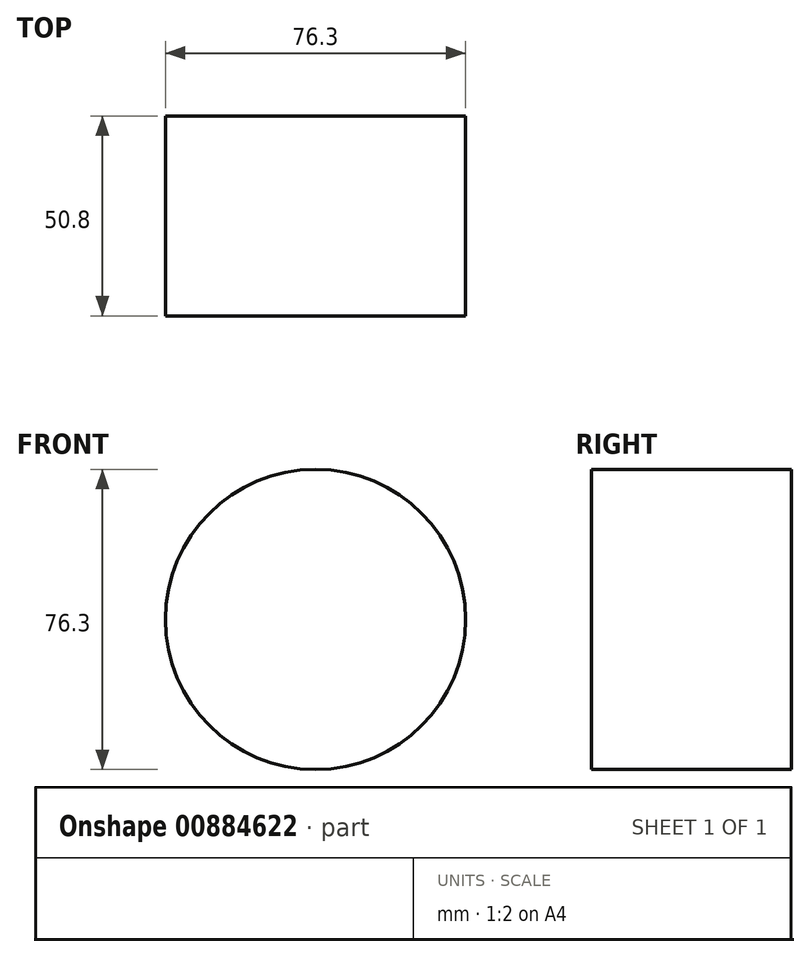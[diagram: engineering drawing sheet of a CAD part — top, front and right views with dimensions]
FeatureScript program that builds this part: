
annotation { "Feature Type Name" : "Feature", "Feature Type Description" : "" }
export const myFeature = defineFeature(function(context is Context, id is Id, definition is map)
    precondition{}
    {
        {
            var Q0;
            Q0=qCreatedBy(makeId("Front.planeOp"),FACE);
            var sketch = newSketch(context, id + "F0", { "sketchPlane" : qUnion([Q0])});
            skCircle(sketch, "E0", {"center": v(0, 0) * mm, "radius": 38.15 * mm});
            skSolve(sketch);
        }
        {
            var Q0;
            Q0 = qSketchRegion(id + "F0", true);
            extrude(context, id + "F1", {"entities" : qUnion([Q0]), "depth" : 50.8 * mm, "offsetDistance" : 25.4 * mm});
        }
    });
